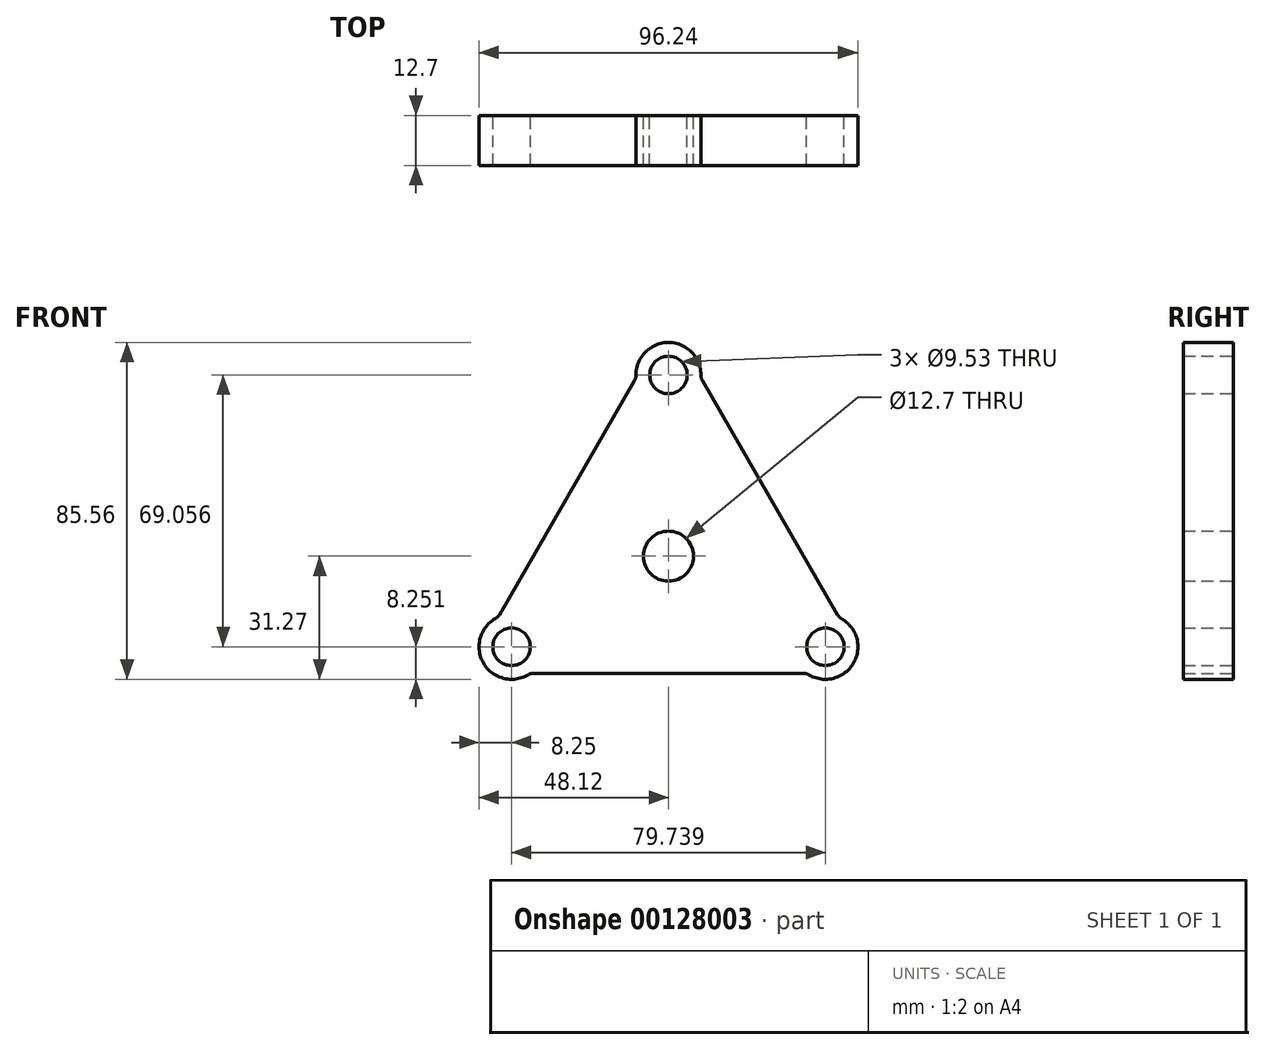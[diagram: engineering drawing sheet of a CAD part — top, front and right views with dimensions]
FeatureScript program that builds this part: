
annotation { "Feature Type Name" : "Feature", "Feature Type Description" : "" }
export const myFeature = defineFeature(function(context is Context, id is Id, definition is map)
    precondition{}
    {
        {
            var Q0;
            Q0=qCreatedBy(makeId("Front.planeOp"),FACE);
            var sketch = newSketch(context, id + "F0", { "sketchPlane" : qUnion([Q0])});
            skCircle(sketch, "E0", {"center": v(0, 0) * mm, "radius": 46.04 * mm, "construction": true});
            skCircle(sketch, "E1", {"center": v(0, 46.04) * mm, "radius": 4.76 * mm});
            skArc(sketch, "E2", {"start": v(8.25, 45.95) * mm, "mid": v(0, 54.3) * mm, "end": v(-8.25, 45.95) * mm});
            skArc(sketch, "E3.1.0", {"start": v(-43.92, -15.83) * mm, "mid": v(-47.02, -27.15) * mm, "end": v(-35.67, -30.12) * mm});
            skCircle(sketch, "E3.1.1", {"center": v(-39.87, -23.02) * mm, "radius": 4.76 * mm});
            skArc(sketch, "E3.2.0", {"start": v(35.67, -30.12) * mm, "mid": v(47.02, -27.15) * mm, "end": v(43.92, -15.83) * mm});
            skCircle(sketch, "E3.2.1", {"center": v(39.87, -23.02) * mm, "radius": 4.76 * mm});
            skLineSegment(sketch, "E4", {"start": v(-42.97, -14.88) * mm, "end": v(-8.6, 44.65) * mm});
            skLineSegment(sketch, "E5", {"start": v(8.6, 44.65) * mm, "end": v(42.97, -14.88) * mm});
            skLineSegment(sketch, "E6", {"start": v(34.37, -29.77) * mm, "end": v(-34.37, -29.77) * mm});
            skPoint(sketch, "E7.visualSharp", {"position": v(-8.22, 45.3) * mm});
            skArc(sketch, "E7.filletArc", {"start": v(-8.6, 44.65) * mm, "mid": v(-8.34, 45.28) * mm, "end": v(-8.25, 45.95) * mm});
            skPoint(sketch, "E8.visualSharp", {"position": v(8.22, 45.3) * mm});
            skArc(sketch, "E8.filletArc", {"start": v(8.25, 45.95) * mm, "mid": v(8.34, 45.28) * mm, "end": v(8.6, 44.65) * mm});
            skPoint(sketch, "E9.visualSharp", {"position": v(43.34, -15.53) * mm});
            skArc(sketch, "E9.filletArc", {"start": v(42.97, -14.88) * mm, "mid": v(43.38, -15.42) * mm, "end": v(43.92, -15.83) * mm});
            skPoint(sketch, "E10.visualSharp", {"position": v(35.12, -29.77) * mm});
            skArc(sketch, "E10.filletArc", {"start": v(35.67, -30.12) * mm, "mid": v(35.04, -29.86) * mm, "end": v(34.37, -29.77) * mm});
            skPoint(sketch, "E11.visualSharp", {"position": v(-35.12, -29.77) * mm});
            skArc(sketch, "E11.filletArc", {"start": v(-34.37, -29.77) * mm, "mid": v(-35.04, -29.86) * mm, "end": v(-35.67, -30.12) * mm});
            skPoint(sketch, "E12.visualSharp", {"position": v(-43.34, -15.53) * mm});
            skArc(sketch, "E12.filletArc", {"start": v(-43.92, -15.83) * mm, "mid": v(-43.38, -15.42) * mm, "end": v(-42.97, -14.88) * mm});
            skCircle(sketch, "E13", {"center": v(0, 0) * mm, "radius": 6.35 * mm});
            skSolve(sketch);
        }
        {
            var Q0;
            Q0=makeQuery(id+"F0.imprint","IMPRINT",FACE,{"disambiguationData":[TD([[makeQuery(id+"F0.imprint","IMPRINT",EDGE,{"derivedFrom":sQuery(id+"F0.wireOp",EDGE,"E1")}),-1.0]])]});
            extrude(context, id + "F1", {"entities" : qUnion([Q0]), "depth" : 12.7 * mm});
        }
    });
